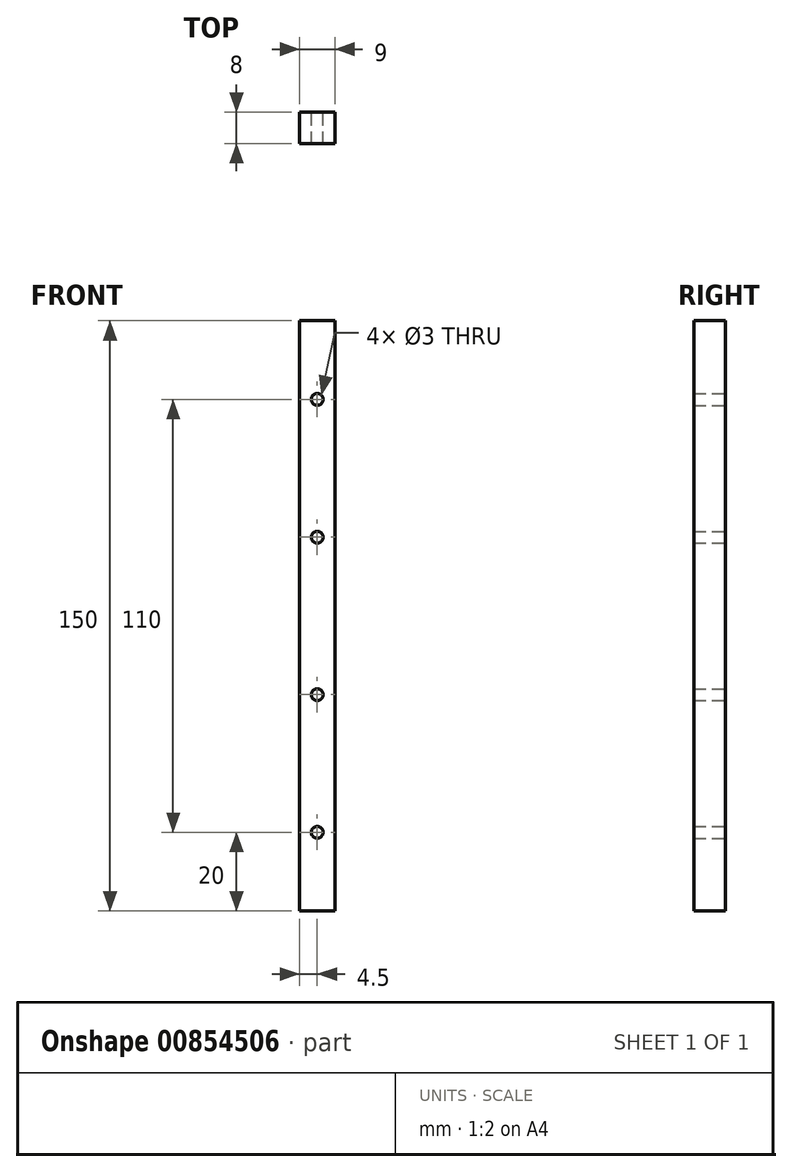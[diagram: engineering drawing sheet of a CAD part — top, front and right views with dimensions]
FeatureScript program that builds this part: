
annotation { "Feature Type Name" : "Feature", "Feature Type Description" : "" }
export const myFeature = defineFeature(function(context is Context, id is Id, definition is map)
    precondition{}
    {
        {
            var Q0;
            Q0=qCreatedBy(makeId("Top.planeOp"),FACE);
            var sketch = newSketch(context, id + "F0", { "sketchPlane" : qUnion([Q0])});
            skLineSegment(sketch, "E0.bottom", {"start": v(4.5, 4) * mm, "end": v(-4.5, 4) * mm});
            skLineSegment(sketch, "E0.top", {"start": v(4.5, -4) * mm, "end": v(-4.5, -4) * mm});
            skLineSegment(sketch, "E0.left", {"start": v(4.5, 4) * mm, "end": v(4.5, -4) * mm});
            skLineSegment(sketch, "E0.right", {"start": v(-4.5, 4) * mm, "end": v(-4.5, -4) * mm});
            skPoint(sketch, "E0.middle", {"position": v(0, 0) * mm});
            skSolve(sketch);
        }
        {
            var Q0;
            Q0 = qSketchRegion(id + "F0", true);
            extrude(context, id + "F1", {"entities" : qUnion([Q0]), "depth" : 150 * mm, "offsetDistance" : 25 * mm});
        }
        {
            var Q0;
            Q0=makeQuery(id+"F1.opExtrude","SWEPT_FACE",FACE,{"disambiguationData":[OSD([sQuery(id+"F0.wireOp",EDGE,"E0.bottom")])]});
            var sketch = newSketch(context, id + "F2", { "sketchPlane" : qUnion([Q0])});
            skCircle(sketch, "E1", {"center": v(0, 20) * mm, "radius": 1.5 * mm});
            skPoint(sketch, "E1.centerSnap0", {"position": v(0, 0) * mm});
            skCircle(sketch, "E2", {"center": v(0, 55) * mm, "radius": 1.5 * mm});
            skCircle(sketch, "E3.MirrorC", {"center": v(0, 95) * mm, "radius": 1.5 * mm});
            skCircle(sketch, "E4.MirrorC", {"center": v(0, 130) * mm, "radius": 1.5 * mm});
            skSolve(sketch);
        }
        {
            var Q0;
            Q0 = qSketchRegion(id + "F2", true);
            extrude(context, id + "F3", {"entities" : qUnion([Q0]), "operationType" : NewBodyOperationType.REMOVE, "oppositeDirection" : true, "depth" : 9 * mm, "offsetDistance" : 25 * mm});
        }
    });
